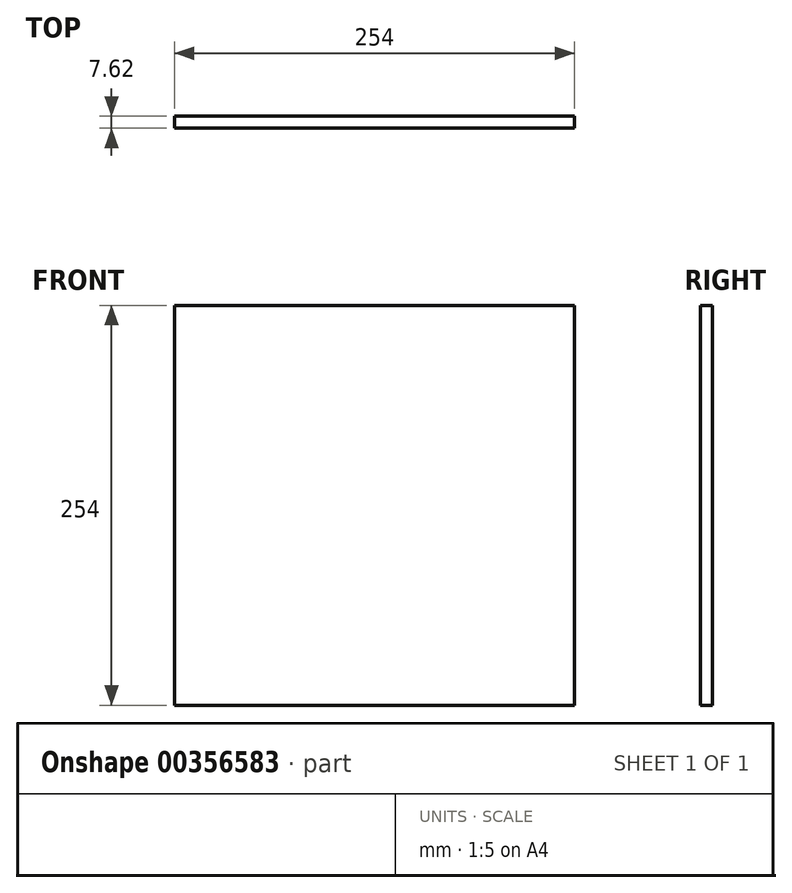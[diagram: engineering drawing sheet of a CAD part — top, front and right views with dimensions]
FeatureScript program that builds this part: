
annotation { "Feature Type Name" : "Feature", "Feature Type Description" : "" }
export const myFeature = defineFeature(function(context is Context, id is Id, definition is map)
    precondition{}
    {
        {
            var Q0;
            Q0=qCreatedBy(makeId("Front.planeOp"),FACE);
            var sketch = newSketch(context, id + "F0", { "sketchPlane" : qUnion([Q0])});
            skLineSegment(sketch, "E0.bottom", {"start": v(-127, 127) * mm, "end": v(127, 127) * mm});
            skLineSegment(sketch, "E0.top", {"start": v(-127, -127) * mm, "end": v(127, -127) * mm});
            skLineSegment(sketch, "E0.left", {"start": v(-127, 127) * mm, "end": v(-127, -127) * mm});
            skLineSegment(sketch, "E0.right", {"start": v(127, 127) * mm, "end": v(127, -127) * mm});
            skPoint(sketch, "E0.middle", {"position": v(0, 0) * mm});
            skSolve(sketch);
        }
        {
            var Q0;
            Q0=makeQuery(id+"F0.imprint","IMPRINT",FACE,{"disambiguationData":[TD([[makeQuery(id+"F0.imprint","IMPRINT",EDGE,{"derivedFrom":sQuery(id+"F0.wireOp",EDGE,"E0.bottom")}),-1.0]])]});
            extrude(context, id + "F1", {"entities" : qUnion([Q0]), "depth" : 7.62 * mm});
        }
    });
